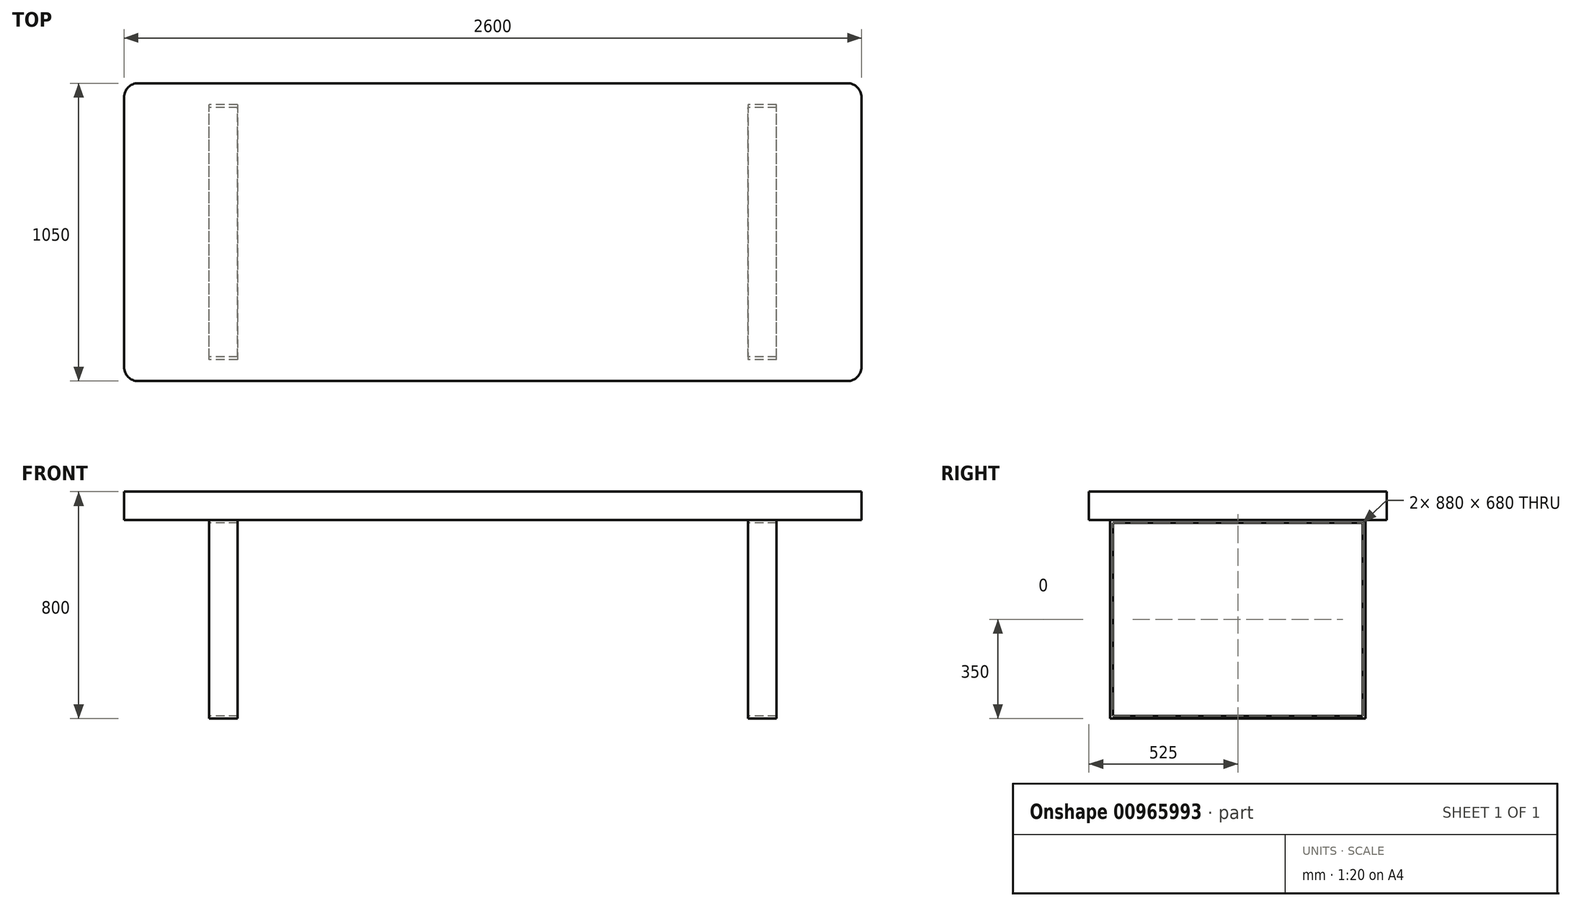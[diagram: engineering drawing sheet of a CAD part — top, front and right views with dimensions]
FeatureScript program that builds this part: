
annotation { "Feature Type Name" : "Feature", "Feature Type Description" : "" }
export const myFeature = defineFeature(function(context is Context, id is Id, definition is map)
    precondition{}
    {
        {
            var Q0;
            Q0=qCreatedBy(makeId("Top.planeOp"),FACE);
            var sketch = newSketch(context, id + "F0", { "sketchPlane" : qUnion([Q0])});
            skLineSegment(sketch, "E0.bottom", {"start": v(-1300, 525) * mm, "end": v(1300, 525) * mm});
            skLineSegment(sketch, "E0.top", {"start": v(-1300, -525) * mm, "end": v(1300, -525) * mm});
            skLineSegment(sketch, "E0.left", {"start": v(-1300, 525) * mm, "end": v(-1300, -525) * mm});
            skLineSegment(sketch, "E0.right", {"start": v(1300, 525) * mm, "end": v(1300, -525) * mm});
            skLineSegment(sketch, "E1", {"start": v(-1300, 525) * mm, "end": v(1300, -525) * mm, "construction": true});
            skSolve(sketch);
        }
        {
            var Q0;
            Q0 = qSketchRegion(id + "F0", true);
            extrude(context, id + "F1", {"entities" : qUnion([Q0]), "depth" : 100 * mm, "offsetDistance" : 25 * mm});
        }
        {
            var Q0;
            Q0=qCreatedBy(makeId("Right.planeOp"),FACE);
            var sketch = newSketch(context, id + "F2", { "sketchPlane" : qUnion([Q0])});
            skLineSegment(sketch, "E2.bottom", {"start": v(-450, 0) * mm, "end": v(450, 0) * mm});
            skLineSegment(sketch, "E2.top", {"start": v(-450, -700) * mm, "end": v(450, -700) * mm});
            skLineSegment(sketch, "E2.left", {"start": v(-450, 0) * mm, "end": v(-450, -700) * mm});
            skLineSegment(sketch, "E2.right", {"start": v(450, 0) * mm, "end": v(450, -700) * mm});
            skLineSegment(sketch, "E3.0", {"start": v(-440, -690) * mm, "end": v(440, -690) * mm});
            skLineSegment(sketch, "E3.1", {"start": v(-440, -10) * mm, "end": v(-440, -690) * mm});
            skLineSegment(sketch, "E3.2", {"start": v(-440, -10) * mm, "end": v(440, -10) * mm});
            skLineSegment(sketch, "E3.3", {"start": v(440, -10) * mm, "end": v(440, -690) * mm});
            skSolve(sketch);
        }
        {
            var Q0;
            Q0 = qSketchRegion(id + "F2", true);
            extrude(context, id + "F3", {"entities" : qUnion([Q0]), "operationType" : NewBodyOperationType.ADD, "endBound" : BoundingType.SYMMETRIC, "depth" : 2000 * mm, "offsetDistance" : 25 * mm});
        }
        {
            var Q0;
            Q0=qCreatedBy(makeId("Front.planeOp"),FACE);
            var sketch = newSketch(context, id + "F4", { "sketchPlane" : qUnion([Q0])});
            skLineSegment(sketch, "E4.bottom", {"start": v(-900, -700) * mm, "end": v(900, -700) * mm});
            skLineSegment(sketch, "E4.top", {"start": v(-900, 0) * mm, "end": v(900, 0) * mm});
            skLineSegment(sketch, "E4.left", {"start": v(-900, -700) * mm, "end": v(-900, 0) * mm});
            skLineSegment(sketch, "E4.right", {"start": v(900, -700) * mm, "end": v(900, 0) * mm});
            skSolve(sketch);
        }
        {
            var Q0;
            Q0 = qSketchRegion(id + "F4", true);
            extrude(context, id + "F5", {"entities" : qUnion([Q0]), "operationType" : NewBodyOperationType.REMOVE, "endBound" : BoundingType.THROUGH_ALL, "oppositeDirection" : true, "depth" : 25 * mm, "offsetDistance" : 25 * mm, "hasSecondDirection" : true, "secondDirectionBound" : SecondDirectionBoundingType.THROUGH_ALL, "secondDirectionOppositeDirection" : false, "secondDirectionDepth" : 25 * mm});
        }
        {
            var Q0;
            Q0=makeQuery(id+"F1.opExtrude","SWEPT_EDGE",EDGE,{"disambiguationData":[OSD([sQuery(id+"F0.wireOp",EDGE,"E0.top"),sQuery(id+"F0.wireOp",EDGE,"E0.right")])]});
            var Q1;
            Q1=makeQuery(id+"F1.opExtrude","SWEPT_EDGE",EDGE,{"disambiguationData":[OSD([sQuery(id+"F0.wireOp",EDGE,"E0.bottom"),sQuery(id+"F0.wireOp",EDGE,"E0.right")])]});
            var Q2;
            Q2=makeQuery(id+"F1.opExtrude","SWEPT_EDGE",EDGE,{"disambiguationData":[OSD([sQuery(id+"F0.wireOp",EDGE,"E0.bottom"),sQuery(id+"F0.wireOp",EDGE,"E0.left")])]});
            var Q3;
            Q3=makeQuery(id+"F1.opExtrude","SWEPT_EDGE",EDGE,{"disambiguationData":[OSD([sQuery(id+"F0.wireOp",EDGE,"E0.top"),sQuery(id+"F0.wireOp",EDGE,"E0.left")])]});
            fillet(context, id + "F6", {"entities" : qUnion([Q0, Q1, Q2, Q3]), "radius" : 50 * mm, "tangentPropagation" : true, "allowEdgeOverflow" : false});
        }
    });
